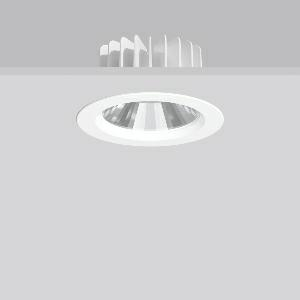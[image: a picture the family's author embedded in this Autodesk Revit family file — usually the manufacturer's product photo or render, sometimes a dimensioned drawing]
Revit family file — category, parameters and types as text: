
# Revit family: ledona_round_ip65_901526_002_2_76_f98b
name_source: partatom
category: Lighting Fixtures
units: mm (PartAtom-declared; Revit-internal decimal feet)

## family parameters
Cut with Voids When Loaded = No
Host = Face
Light Source = No
Part Type = Normal
Room Calculation Point = No
Round Connector Dimension = Use Diameter
Shared = No

## types (1)
- TuneableWhite 846 (1 x LED Modul 846, 2450 lm, 4600)
    Apparent Load = 30 VA
    CIE Flux Codes = 88 100 100 100 100
    Color Rendering = 80
    Color Temperature = 4600
    Default Elevation = 1800 mm
    Height = 0 mm  [stored 0 ft]
    Lamp = 1 x LED Modul 846
    Lamp Light Flux = 2450 lm
    Lamp count = 1
    Length = 180 mm  [stored 0.590551 ft]
    Lifetime = 50000 h
    Luminous efficacy = 82 lm/W
    Manufacturer = RZB
    ModVariant = No
    Model = 901526.002.2.76
    Mounting Place = Ceiling
    Mounting Type = Recessed
    Number of Poles = 1
    OnlyDefault = Yes
    Power Factor = 1
    Product Name = LEDONA round IP65
    Product group = Recessed downlights
    ProductGroupID = 402
    Protection Class = Protection class II
    Protection Degree = IP 65
    RLX_Detail_Level = 1
    RLX_Emergency_Light_Flux = 0 lm
    RLX_Emergency_Type = 0
    RLX_Emergency_Type_DB = No
    RlxData = <blob elided: 38769 chars, md5=9c0246d0>
    Socket = socket
    Standby Power = 0 W
    System Light Flux = 2450 lm
    System Power = 30 W
    Type Comments = TuneableWhite 846
    Type Image = 901346.002.jpg
    URL = http://relux.com
    VarID = tuneablewhite_846
    Voltage = 230 V
    Voltage Range = 220-240 V
    Weight = 0.00 kg
    Width = 0 mm  [stored 0 ft]

note: [stored X ft] marks values corroborated as IEEE doubles in the binary element streams (Revit-internal decimal feet)

## geometry (parser evidence)
native form markers: Blend x4, Sweep x10
no freeform markers — native parametric forms only
